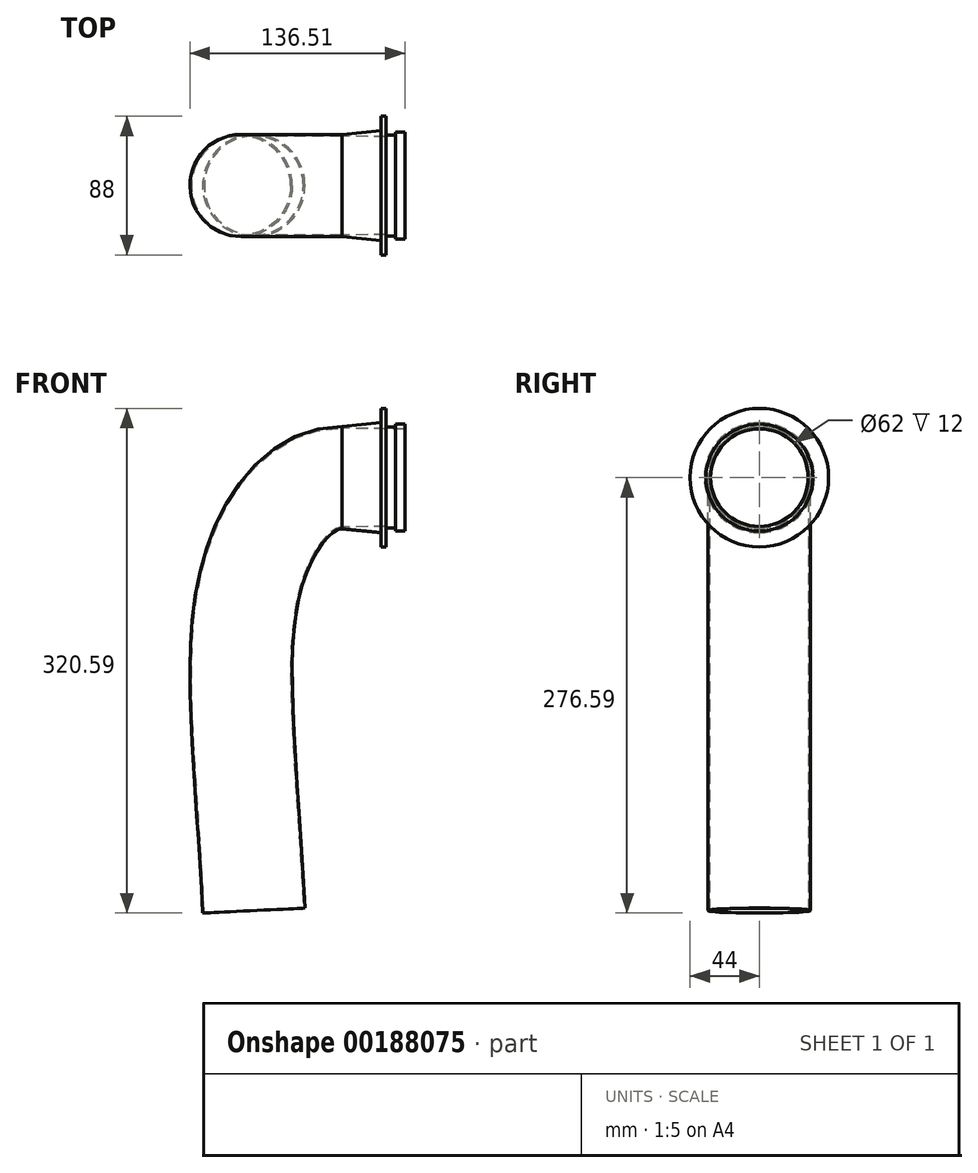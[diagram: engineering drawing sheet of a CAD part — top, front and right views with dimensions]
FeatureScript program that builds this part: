
annotation { "Feature Type Name" : "Feature", "Feature Type Description" : "" }
export const myFeature = defineFeature(function(context is Context, id is Id, definition is map)
    precondition{}
    {
        {
            var Q0;
            Q0=qCreatedBy(makeId("Front.planeOp"),FACE);
            var sketch = newSketch(context, id + "F0", { "sketchPlane" : qUnion([Q0])});
            skLineSegment(sketch, "E0", {"start": v(-106.4, 0) * mm, "end": v(156.4, 0) * mm, "construction": true});
            skLineSegment(sketch, "E1", {"start": v(0, 0) * mm, "end": v(0, 34) * mm});
            skLineSegment(sketch, "E2", {"start": v(0, 34) * mm, "end": v(-6, 34) * mm});
            skLineSegment(sketch, "E3", {"start": v(-6, 34) * mm, "end": v(-6, 31) * mm});
            skLineSegment(sketch, "E4", {"start": v(-6, 31) * mm, "end": v(0, 31) * mm});
            skLineSegment(sketch, "E5", {"start": v(-6, 32) * mm, "end": v(-12, 32) * mm});
            skLineSegment(sketch, "E6", {"start": v(-6, 31) * mm, "end": v(-12, 31) * mm});
            skLineSegment(sketch, "E7", {"start": v(-12, 44) * mm, "end": v(-15, 44) * mm});
            skLineSegment(sketch, "E8", {"start": v(-12, 44) * mm, "end": v(-12, 32) * mm});
            skLineSegment(sketch, "E9", {"start": v(-15, 44) * mm, "end": v(-15, 35) * mm});
            skLineSegment(sketch, "E10", {"start": v(-15, 35) * mm, "end": v(-40, 32.5) * mm});
            skLineSegment(sketch, "E11", {"start": v(-95, 32.5) * mm, "end": v(-95, 31.5) * mm});
            skLineSegment(sketch, "E12", {"start": v(-95, 32.5) * mm, "end": v(-95, 0) * mm});
            skLineSegment(sketch, "E13", {"start": v(-40, 32.5) * mm, "end": v(-40, 0) * mm});
            skLineSegment(sketch, "E14", {"start": v(-40, 32.5) * mm, "end": v(-40, 31.5) * mm});
            skLineSegment(sketch, "E15", {"start": v(-40, 31.5) * mm, "end": v(-12, 31) * mm});
            skSolve(sketch);
        }
        {
            var Q0;
            {var subQ4=sQuery(id+"F0.wireOp",EDGE,"E5");Q0=makeQuery(id+"F0.imprint","IMPRINT",FACE,{"disambiguationData":[TD([[makeQuery(id+"F0.imprint","IMPRINT",EDGE,{"derivedFrom":subQ4}),1.0]])]});}
            var Q1;
            {var subQ3=sQuery(id+"F0.wireOp",EDGE,"E2");Q1=makeQuery(id+"F0.imprint","IMPRINT",FACE,{"disambiguationData":[TD([[makeQuery(id+"F0.imprint","IMPRINT",EDGE,{"derivedFrom":subQ3}),1.0]])]});}
            var Q2;
            Q2=sQuery(id+"F0.wireOp",EDGE,"E0");
            revolve(context, id + "F1", {"entities" : qUnion([Q0, Q1]), "axis" : qUnion([Q2]), "revolveType" : RevolveType.FULL});
        }
        {
            var Q0;
            Q0=qCreatedBy(makeId("Right.planeOp"),FACE);
            cPlane(context, id + "F2", {"entities" : qUnion([Q0]), "cplaneType" : CPlaneType.OFFSET, "offset" : 40 * mm, "oppositeDirection" : true, "width" : 150 * mm, "height" : 150 * mm});
        }
        {
            var Q0;
            Q0=qCreatedBy(makeId("Front.planeOp"),FACE);
            var sketch = newSketch(context, id + "F3", { "sketchPlane" : qUnion([Q0])});
            skPoint(sketch, "E16", {"position": v(0, 0) * mm});
            skPoint(sketch, "E17", {"position": v(-40, 0) * mm});
            skPoint(sketch, "E18.endSnap0", {"position": v(-95, -55) * mm});
            skPoint(sketch, "E19", {"position": v(-95.93, -275) * mm});
            skFitSpline(sketch, "E20", {"points": [v(-40, 0) * mm, v(-95, -55) * mm, v(-95.93, -275) * mm], "startDerivative": vector(-204.49, 0) * mm, "endDerivative": vector(24.25, -496.5) * mm});
            skSolve(sketch);
        }
        {
            var Q0;
            Q0=qCreatedBy(id+"F2.planeOp",FACE);
            var sketch = newSketch(context, id + "F4", { "sketchPlane" : qUnion([Q0])});
            skCircle(sketch, "E21", {"center": v(0, 0) * mm, "radius": 31.5 * mm});
            skCircle(sketch, "E22", {"center": v(0, 0) * mm, "radius": 32.5 * mm});
            skSolve(sketch);
        }
        {
            var Q0;
            Q0 = qSketchRegion(id + "F4", true);
            var Q1;
            Q1=sQuery(id+"F3.wireOp",EDGE,"E20");
            sweep(context, id + "F5", {"operationType" : NewBodyOperationType.ADD, "profiles" : qUnion([Q0]), "path" : qUnion([Q1])});
        }
    });
